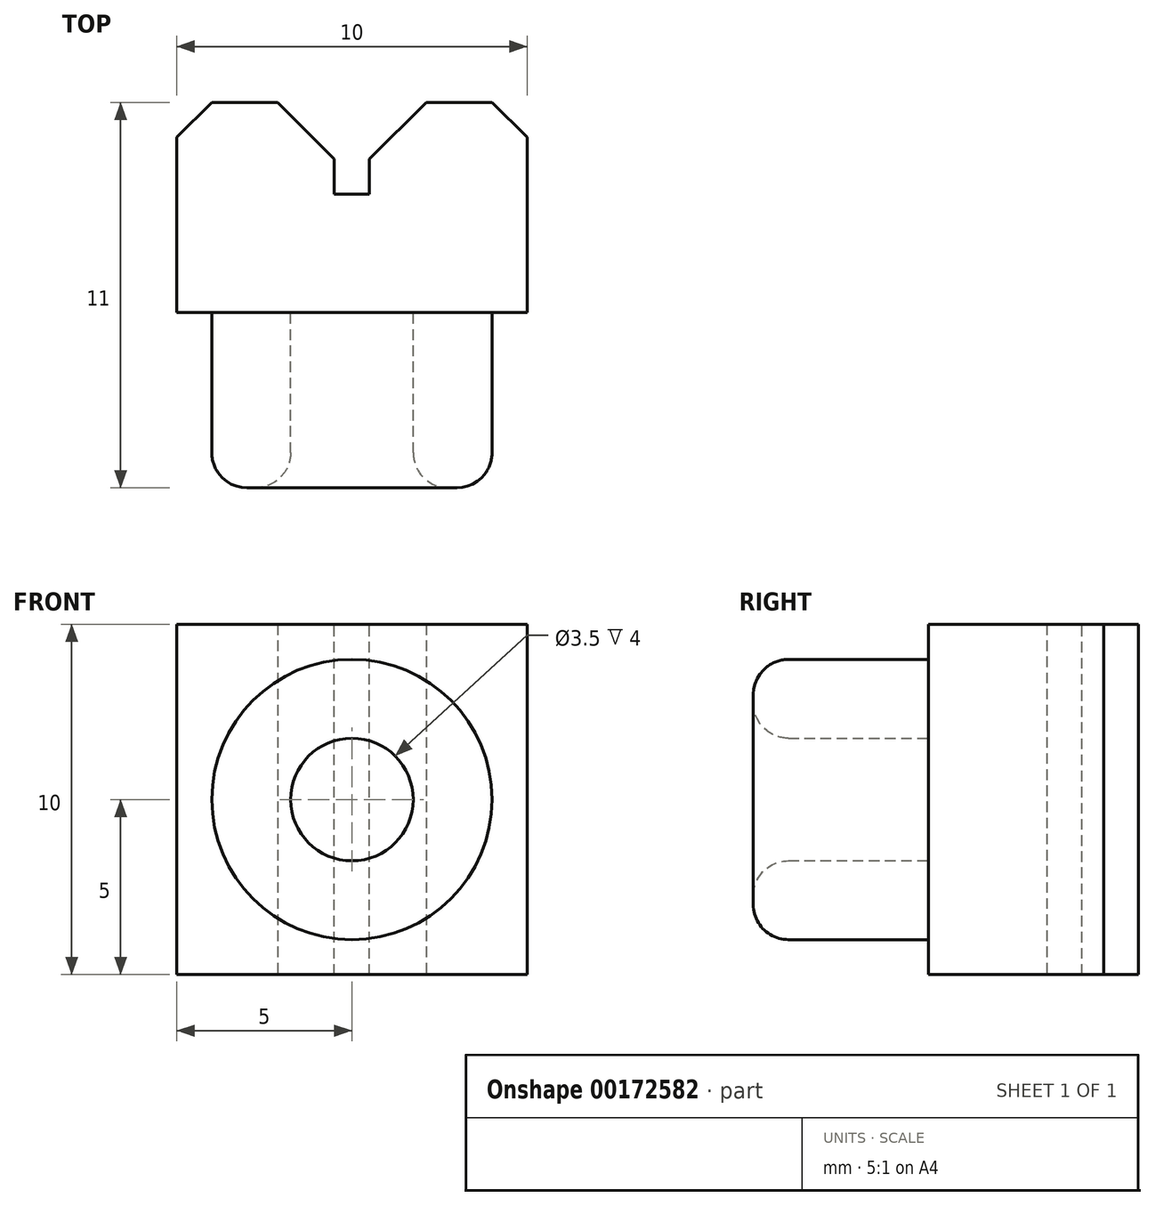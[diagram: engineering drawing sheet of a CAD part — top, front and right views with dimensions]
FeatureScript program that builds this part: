
annotation { "Feature Type Name" : "Feature", "Feature Type Description" : "" }
export const myFeature = defineFeature(function(context is Context, id is Id, definition is map)
    precondition{}
    {
        {
            var Q0;
            Q0=qCreatedBy(makeId("Top.planeOp"),FACE);
            var sketch = newSketch(context, id + "F0", { "sketchPlane" : qUnion([Q0])});
            skLineSegment(sketch, "E0", {"start": v(0, 0) * mm, "end": v(10, 0) * mm});
            skLineSegment(sketch, "E1", {"start": v(10, 0) * mm, "end": v(10, 6) * mm});
            skLineSegment(sketch, "E2", {"start": v(10, 6) * mm, "end": v(7.12, 6) * mm});
            skLineSegment(sketch, "E3", {"start": v(7.12, 6) * mm, "end": v(5, 3.88) * mm});
            skPoint(sketch, "E3.endSnap0", {"position": v(5, 0) * mm});
            skLineSegment(sketch, "E4", {"start": v(5, 3.88) * mm, "end": v(2.88, 6) * mm});
            skLineSegment(sketch, "E5", {"start": v(2.88, 6) * mm, "end": v(0, 6) * mm});
            skLineSegment(sketch, "E6", {"start": v(0, 6) * mm, "end": v(0, 0) * mm});
            skSolve(sketch);
        }
        {
            var Q0;
            Q0 = qSketchRegion(id + "F0", true);
            extrude(context, id + "F1", {"entities" : qUnion([Q0]), "depth" : 10 * mm});
        }
        {
            var Q0;
            Q0=makeQuery(id+"F1.opExtrude","SWEPT_FACE",FACE,{"disambiguationData":[OSD([sQuery(id+"F0.wireOp",EDGE,"E0")])]});
            var sketch = newSketch(context, id + "F2", { "sketchPlane" : qUnion([Q0])});
            skCircle(sketch, "E7", {"center": v(5, 5) * mm, "radius": 1.75 * mm});
            skPoint(sketch, "E7.centerSnap0", {"position": v(5, 10) * mm});
            skPoint(sketch, "E7.centerSnap1", {"position": v(0, 5) * mm});
            skCircle(sketch, "E8", {"center": v(5, 5) * mm, "radius": 4 * mm});
            skSolve(sketch);
        }
        {
            var Q0;
            Q0 = qSketchRegion(id + "F2", true);
            extrude(context, id + "F3", {"entities" : qUnion([Q0]), "operationType" : NewBodyOperationType.ADD, "depth" : 5 * mm});
        }
        {
            var Q0;
            Q0=makeQuery(id+"F1.opExtrude","SWEPT_EDGE",EDGE,{"disambiguationData":[OSD([sQuery(id+"F0.wireOp",EDGE,"E1"),sQuery(id+"F0.wireOp",EDGE,"E2")])]});
            var Q1;
            Q1=makeQuery(id+"F1.opExtrude","SWEPT_EDGE",EDGE,{"disambiguationData":[OSD([sQuery(id+"F0.wireOp",EDGE,"E5"),sQuery(id+"F0.wireOp",EDGE,"E6")])]});
            chamfer(context, id + "F4", {"entities" : qUnion([Q0, Q1]), "width" : 1 * mm, "tangentPropagation" : true});
        }
        {
            var Q0;
            Q0=makeQuery(id+"F1.opExtrude","CAP_FACE",FACE,{"disambiguationData":[OSD([sQuery(id+"F0.wireOp",EDGE,"E0"),sQuery(id+"F0.wireOp",EDGE,"E1"),sQuery(id+"F0.wireOp",EDGE,"E2"),sQuery(id+"F0.wireOp",EDGE,"E3"),sQuery(id+"F0.wireOp",EDGE,"E4"),sQuery(id+"F0.wireOp",EDGE,"E5"),sQuery(id+"F0.wireOp",EDGE,"E6")])],"isStart":true});
            var sketch = newSketch(context, id + "F5", { "sketchPlane" : qUnion([Q0])});
            skLineSegment(sketch, "E9.bottom", {"start": v(5.5, -5.77) * mm, "end": v(4.5, -5.77) * mm});
            skLineSegment(sketch, "E9.top", {"start": v(5.5, -3.38) * mm, "end": v(4.5, -3.38) * mm});
            skLineSegment(sketch, "E9.left", {"start": v(5.5, -5.77) * mm, "end": v(5.5, -3.38) * mm});
            skLineSegment(sketch, "E9.right", {"start": v(4.5, -5.77) * mm, "end": v(4.5, -3.38) * mm});
            skSolve(sketch);
        }
        {
            var Q0;
            Q0 = qSketchRegion(id + "F5", true);
            extrude(context, id + "F6", {"entities" : qUnion([Q0]), "operationType" : NewBodyOperationType.REMOVE, "oppositeDirection" : true, "depth" : 25 * mm});
        }
        {
            var Q0;
            Q0=makeQuery(id+"F3.opExtrude","CAP_EDGE",EDGE,{"disambiguationData":[OSD([sQuery(id+"F2.wireOp",EDGE,"E8")])],"isStart":true});
            var Q1;
            Q1=makeQuery(id+"F3.opExtrude","CAP_EDGE",EDGE,{"disambiguationData":[OSD([sQuery(id+"F2.wireOp",EDGE,"E8")])],"isStart":false});
            var Q2;
            Q2=makeQuery(id+"F3.opExtrude","CAP_EDGE",EDGE,{"disambiguationData":[OSD([sQuery(id+"F2.wireOp",EDGE,"E7")])],"isStart":false});
            fillet(context, id + "F7", {"entities" : qUnion([Q0, Q1, Q2]), "radius" : 1 * mm, "tangentPropagation" : true, "allowEdgeOverflow" : false});
        }
    });
